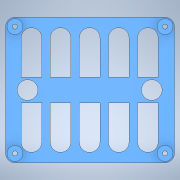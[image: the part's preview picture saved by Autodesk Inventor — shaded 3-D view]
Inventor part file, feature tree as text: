
AUTODESK INVENTOR PART (.ipt)
format: ipt  version: 2022 (Build 260153000, 153)  size: 254,464 bytes
history: native  units: mm
features: extrude x5, sketch x5, plane x2, hole x1
ambient origin geometry x8: Origin, YZ Plane, XZ Plane, XY Plane, X Axis, Y Axis, Z Axis, Center Point
bodies: Solid1 (feature_tree)
feature tree (13):
  extrude  "Extrusion1"  Depth=6.2mm
  extrude  "Extrusion2"  Depth=6.2mm
  extrude  "Extrusion3"  Depth=58.0mm
  hole  "Hole1"  [1 undecoded]
  sketch  "Sketch7"  dims[d16=2.0mm d17=0.0mm d18=7.25mm d19=7.25mm d20=7.25mm d21=7.25mm d22=2.0mm d23=0.0mm d27=8.0mm d28=8.0mm d29=8.0mm d30=8.0mm d31=10.0mm d32=10.0mm d33=50.0mm d35=11.25mm d36=10.0mm d38=10.0mm d40=2.0mm d41=0.0mm d42=2.0mm d43=6.0mm d44=4.0mm d45=2.0mm d46=90.0deg d47=8.0mm d48=20.594885mm d49=8.0mm d50=8.0mm d51=48.0mm d52=8.5mm d55=10.0mm d56=5.0mm d57=10.0mm d58=0.0mm d59=10.0mm d60=0.0mm d61=0.5mm d62=0.872665mm]
  plane  "Work Plane2"
  extrude  "Extrusion5"  Depth=10.0mm
  plane  "Work Plane1"
  extrude  "Extrusion6"  Depth=10.0mm
  sketch  "Sketch1"  dims[d4=6.2mm d5=6.2mm]
  sketch  "Sketch3"  dims[d6=6.2mm d7=6.2mm]
  sketch  "Sketch5"  dims[d12=58.0mm d13=58.0mm]
  sketch  "Sketch6"  dims[d14=49.0mm d15=49.0mm]
note: 1 required parameter value undecoded (feature->parameter linkage not recoverable at this tier; creation-order binding heuristic only, values carry confidence <= 0.55)
